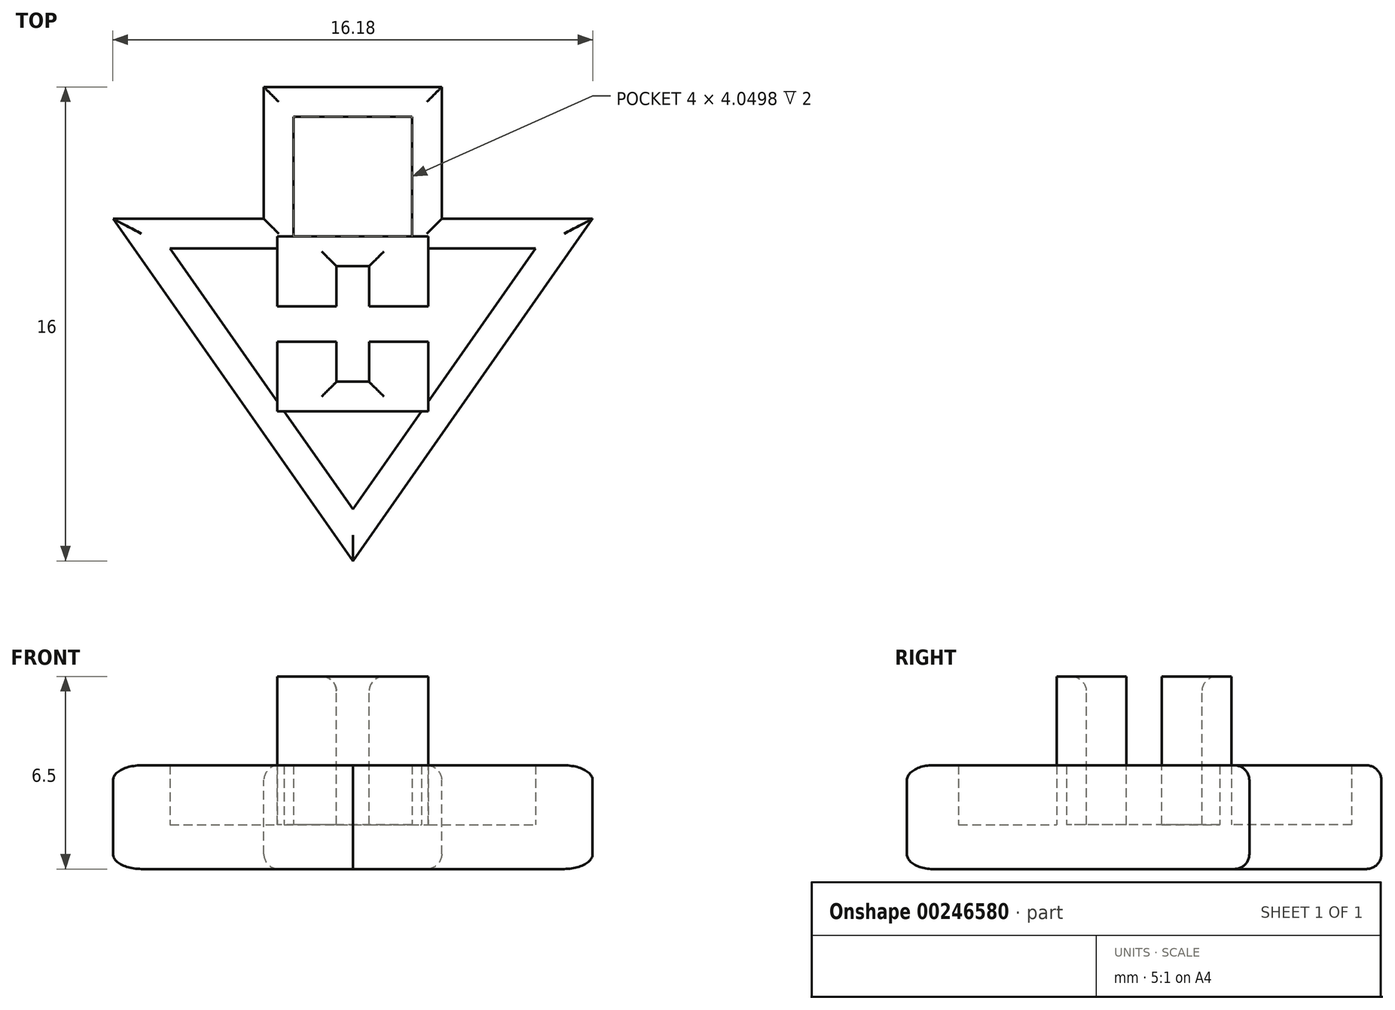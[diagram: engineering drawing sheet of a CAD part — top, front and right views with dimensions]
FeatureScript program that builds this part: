
annotation { "Feature Type Name" : "Feature", "Feature Type Description" : "" }
export const myFeature = defineFeature(function(context is Context, id is Id, definition is map)
    precondition{}
    {
        {
            var Q0;
            Q0=qCreatedBy(makeId("Top.planeOp"),FACE);
            var sketch = newSketch(context, id + "F0", { "sketchPlane" : qUnion([Q0])});
            skLineSegment(sketch, "E0.bottom", {"start": v(-0.55, 1.95) * mm, "end": v(0.55, 1.95) * mm});
            skLineSegment(sketch, "E0.top", {"start": v(-0.55, -1.95) * mm, "end": v(0.55, -1.95) * mm});
            skLineSegment(sketch, "E0.left", {"start": v(-2, 0.6) * mm, "end": v(-2, -0.6) * mm});
            skLineSegment(sketch, "E0.right", {"start": v(2, 0.6) * mm, "end": v(2, -0.6) * mm});
            skPoint(sketch, "E0.middle", {"position": v(0, 0) * mm});
            skLineSegment(sketch, "E1.left", {"start": v(-0.55, 1.95) * mm, "end": v(-0.55, 0.6) * mm});
            skLineSegment(sketch, "E1.right", {"start": v(0.55, 1.95) * mm, "end": v(0.55, 0.6) * mm});
            skLineSegment(sketch, "E2.bottom", {"start": v(-2, 0.6) * mm, "end": v(-0.55, 0.6) * mm});
            skLineSegment(sketch, "E2.top", {"start": v(-2, -0.6) * mm, "end": v(-0.55, -0.6) * mm});
            skLineSegment(sketch, "E3.trimOffspring", {"start": v(-0.55, -0.6) * mm, "end": v(-0.55, -1.95) * mm});
            skLineSegment(sketch, "E4.trimOffspring", {"start": v(0.55, 0.6) * mm, "end": v(2, 0.6) * mm});
            skLineSegment(sketch, "E5.trimOffspring", {"start": v(0.55, -0.6) * mm, "end": v(0.55, -1.95) * mm});
            skLineSegment(sketch, "E6.trimOffspring", {"start": v(0.55, -0.6) * mm, "end": v(2, -0.6) * mm});
            skPoint(sketch, "E7.orphan", {"position": v(-2, 1.95) * mm});
            skPoint(sketch, "E8.orphan", {"position": v(2, 1.95) * mm});
            skPoint(sketch, "E9.orphan", {"position": v(2, -1.95) * mm});
            skPoint(sketch, "E10.orphan", {"position": v(-2, -1.95) * mm});
            skLineSegment(sketch, "E11", {"start": v(-2, 0.6) * mm, "end": v(-2.55, 0.6) * mm});
            skLineSegment(sketch, "E12", {"start": v(-2.55, 0.6) * mm, "end": v(-2.55, 2.95) * mm});
            skLineSegment(sketch, "E13", {"start": v(-2.55, 2.95) * mm, "end": v(0, 2.95) * mm});
            skLineSegment(sketch, "E14.MirrorCS", {"start": v(2.55, 2.95) * mm, "end": v(0, 2.95) * mm});
            skLineSegment(sketch, "E15.MirrorCS", {"start": v(2.55, 0.6) * mm, "end": v(2.55, 2.95) * mm});
            skLineSegment(sketch, "E16.MirrorCS", {"start": v(2, 0.6) * mm, "end": v(2.55, 0.6) * mm});
            skLineSegment(sketch, "E17.MirrorCS", {"start": v(-2, -0.6) * mm, "end": v(-2.55, -0.6) * mm});
            skLineSegment(sketch, "E18.MirrorCS", {"start": v(-2.55, -0.6) * mm, "end": v(-2.55, -2.95) * mm});
            skLineSegment(sketch, "E19.MirrorCS", {"start": v(-2.55, -2.95) * mm, "end": v(0, -2.95) * mm});
            skLineSegment(sketch, "E20.MirrorCS", {"start": v(2.55, -2.95) * mm, "end": v(0, -2.95) * mm});
            skLineSegment(sketch, "E21.MirrorCS", {"start": v(2.55, -0.6) * mm, "end": v(2.55, -2.95) * mm});
            skLineSegment(sketch, "E22.MirrorCS", {"start": v(2, -0.6) * mm, "end": v(2.55, -0.6) * mm});
            skSolve(sketch);
        }
        {
            var Q0;
            Q0=makeQuery(id+"F0.imprint","IMPRINT",FACE,{"disambiguationData":[TD([[makeQuery(id+"F0.imprint","IMPRINT",EDGE,{"derivedFrom":sQuery(id+"F0.wireOp",EDGE,"E0.bottom")}),1.0]])]});
            var Q1;
            Q1=makeQuery(id+"F0.imprint","IMPRINT",FACE,{"disambiguationData":[TD([[makeQuery(id+"F0.imprint","IMPRINT",EDGE,{"derivedFrom":sQuery(id+"F0.wireOp",EDGE,"E0.top")}),-1.0]])]});
            extrude(context, id + "F1", {"entities" : qUnion([Q0, Q1]), "oppositeDirection" : true, "depth" : 5 * mm});
        }
        {
            var Q0;
            Q0=makeQuery(id+"F1.opExtrude","CAP_FACE",FACE,{"disambiguationData":[OSD([sQuery(id+"F0.wireOp",EDGE,"E0.top"),sQuery(id+"F0.wireOp",EDGE,"E2.top"),sQuery(id+"F0.wireOp",EDGE,"E3.trimOffspring"),sQuery(id+"F0.wireOp",EDGE,"E5.trimOffspring"),sQuery(id+"F0.wireOp",EDGE,"E6.trimOffspring"),sQuery(id+"F0.wireOp",EDGE,"E17.MirrorCS"),sQuery(id+"F0.wireOp",EDGE,"E18.MirrorCS"),sQuery(id+"F0.wireOp",EDGE,"E19.MirrorCS"),sQuery(id+"F0.wireOp",EDGE,"E20.MirrorCS"),sQuery(id+"F0.wireOp",EDGE,"E21.MirrorCS"),sQuery(id+"F0.wireOp",EDGE,"E22.MirrorCS")])],"isStart":false});
            var sketch = newSketch(context, id + "F2", { "sketchPlane" : qUnion([Q0])});
            skLineSegment(sketch, "E23", {"start": v(0, 0) * mm, "end": v(0, 8) * mm});
            skLineSegment(sketch, "E24", {"start": v(0, 0) * mm, "end": v(0, -8) * mm});
            skLineSegment(sketch, "E25", {"start": v(0, 8) * mm, "end": v(5.6, 0) * mm});
            skPoint(sketch, "E26.endSnap0", {"position": v(2.95, 0) * mm});
            skLineSegment(sketch, "E27", {"start": v(3, -3.55) * mm, "end": v(3, -8) * mm});
            skLineSegment(sketch, "E28", {"start": v(3, -8) * mm, "end": v(0, -8) * mm});
            skLineSegment(sketch, "E29.MirrorCS", {"start": v(-3, -8) * mm, "end": v(0, -8) * mm});
            skLineSegment(sketch, "E30.MirrorCS", {"start": v(-3, -3.55) * mm, "end": v(-3, -8) * mm});
            skLineSegment(sketch, "E31.MirrorCS", {"start": v(0, 8) * mm, "end": v(-5.6, 0) * mm});
            skLineSegment(sketch, "E32", {"start": v(5.6, 0) * mm, "end": v(8.09, -3.55) * mm});
            skLineSegment(sketch, "E33", {"start": v(8.09, -3.55) * mm, "end": v(3, -3.55) * mm});
            skLineSegment(sketch, "E34.MirrorCS", {"start": v(-8.09, -3.55) * mm, "end": v(-3, -3.55) * mm});
            skLineSegment(sketch, "E35.MirrorCS", {"start": v(-5.6, 0) * mm, "end": v(-8.09, -3.55) * mm});
            skPoint(sketch, "E36.orphan", {"position": v(-2.95, -3.55) * mm});
            skPoint(sketch, "E37.orphan", {"position": v(2.95, -3.55) * mm});
            skPoint(sketch, "E26.end.orphan", {"position": v(3, 0) * mm});
            skPoint(sketch, "E38.orphan", {"position": v(-3, 0) * mm});
            skPoint(sketch, "E39.MirrorCS.start.orphan", {"position": v(-5.6, 0) * mm});
            skPoint(sketch, "E40", {"position": v(0, 0) * mm});
            skSolve(sketch);
        }
        {
            var Q0;
            Q0=makeQuery(id+"F2.imprint","IMPRINT",FACE,{"disambiguationData":[TD([[makeQuery(id+"F2.imprint","IMPRINT",EDGE,{"derivedFrom":sQuery(id+"F2.wireOp",EDGE,"E23")}),-1.0]])]});
            var Q1;
            Q1=makeQuery(id+"F2.imprint","IMPRINT",FACE,{"disambiguationData":[TD([[makeQuery(id+"F2.imprint","IMPRINT",EDGE,{"derivedFrom":sQuery(id+"F2.wireOp",EDGE,"E23")}),1.0]])]});
            var Q2;
            Q2=makeQuery(id+"F2.imprint","IMPRINT",FACE,{"disambiguationData":[TD([[makeQuery(id+"F2.imprint","IMPRINT",EDGE,{"derivedFrom":makeQuery(id+"F1.opExtrude","CAP_EDGE",EDGE,{"disambiguationData":[OSD([sQuery(id+"F0.wireOp",EDGE,"E0.top")])],"isStart":false})}),1.0]])]});
            extrude(context, id + "F3", {"entities" : qUnion([Q0, Q1, Q2]), "operationType" : NewBodyOperationType.ADD, "depth" : 1.5 * mm});
        }
        {
            var Q0;
            Q0=makeQuery(id+"F3.opExtrude","CAP_FACE",FACE,{"disambiguationData":[OSD([sQuery(id+"F2.wireOp",EDGE,"E25"),sQuery(id+"F2.wireOp",EDGE,"E27"),sQuery(id+"F2.wireOp",EDGE,"E28"),sQuery(id+"F2.wireOp",EDGE,"E29.MirrorCS"),sQuery(id+"F2.wireOp",EDGE,"E30.MirrorCS"),sQuery(id+"F2.wireOp",EDGE,"E31.MirrorCS"),sQuery(id+"F2.wireOp",EDGE,"E32"),sQuery(id+"F2.wireOp",EDGE,"E33"),sQuery(id+"F2.wireOp",EDGE,"E34.MirrorCS"),sQuery(id+"F2.wireOp",EDGE,"E35.MirrorCS")])],"isStart":true});
            var sketch = newSketch(context, id + "F4", { "sketchPlane" : qUnion([Q0])});
            skLineSegment(sketch, "E41.0.0", {"start": v(-3, 8) * mm, "end": v(-3, 3.55) * mm});
            skLineSegment(sketch, "E41.0.1", {"start": v(-3, 3.55) * mm, "end": v(-8.09, 3.55) * mm});
            skLineSegment(sketch, "E41.0.2", {"start": v(-8.09, 3.55) * mm, "end": v(0, -8) * mm});
            skLineSegment(sketch, "E41.0.3", {"start": v(0, -8) * mm, "end": v(8.09, 3.55) * mm});
            skLineSegment(sketch, "E41.0.4", {"start": v(8.09, 3.55) * mm, "end": v(3, 3.55) * mm});
            skLineSegment(sketch, "E41.0.5", {"start": v(3, 3.55) * mm, "end": v(3, 8) * mm});
            skLineSegment(sketch, "E41.0.6", {"start": v(3, 8) * mm, "end": v(-3, 8) * mm});
            skLineSegment(sketch, "E42.0", {"start": v(0, -6.26) * mm, "end": v(6.17, 2.55) * mm});
            skLineSegment(sketch, "E43.0", {"start": v(-3, 2.55) * mm, "end": v(-6.17, 2.55) * mm});
            skLineSegment(sketch, "E44.0", {"start": v(2, 3.55) * mm, "end": v(2, 7) * mm});
            skLineSegment(sketch, "E45.0", {"start": v(-2, 7) * mm, "end": v(-2, 3.55) * mm});
            skLineSegment(sketch, "E46.0", {"start": v(2, 7) * mm, "end": v(-2, 7) * mm});
            skLineSegment(sketch, "E47.trimOffspring", {"start": v(6.17, 2.55) * mm, "end": v(3, 2.55) * mm});
            skLineSegment(sketch, "E48.trimOffspring", {"start": v(-6.17, 2.55) * mm, "end": v(0, -6.26) * mm});
            skLineSegment(sketch, "E49", {"start": v(2, 3.55) * mm, "end": v(2, 2.55) * mm});
            skLineSegment(sketch, "E50", {"start": v(2, 2.55) * mm, "end": v(3, 2.55) * mm});
            skLineSegment(sketch, "E51", {"start": v(-2, 3.55) * mm, "end": v(-2, 2.55) * mm});
            skLineSegment(sketch, "E52", {"start": v(-2, 2.55) * mm, "end": v(-3, 2.55) * mm});
            skSolve(sketch);
        }
        {
            var Q0;
            Q0=makeQuery(id+"F4.imprint","IMPRINT",FACE,{"disambiguationData":[TD([[makeQuery(id+"F4.imprint","IMPRINT",EDGE,{"derivedFrom":sQuery(id+"F4.wireOp",EDGE,"E41.0.0")}),-1.0]])]});
            extrude(context, id + "F5", {"entities" : qUnion([Q0]), "operationType" : NewBodyOperationType.ADD, "depth" : 2 * mm});
        }
        {
            var Q0;
            Q0=makeQuery(id+"F3.opExtrude","CAP_EDGE",EDGE,{"disambiguationData":[OSD([sQuery(id+"F2.wireOp",EDGE,"E33")])],"isStart":false});
            var Q1;
            Q1=makeQuery(id+"F3.opExtrude","CAP_EDGE",EDGE,{"disambiguationData":[OSD([sQuery(id+"F2.wireOp",EDGE,"E27")])],"isStart":false});
            var Q2;
            Q2=makeQuery(id+"F3.opExtrude","CAP_EDGE",EDGE,{"disambiguationData":[OSD([sQuery(id+"F2.wireOp",EDGE,"E28"),sQuery(id+"F2.wireOp",EDGE,"E29.MirrorCS")])],"isStart":false});
            var Q3;
            Q3=makeQuery(id+"F3.opExtrude","CAP_EDGE",EDGE,{"disambiguationData":[OSD([sQuery(id+"F2.wireOp",EDGE,"E30.MirrorCS")])],"isStart":false});
            var Q4;
            Q4=makeQuery(id+"F3.opExtrude","CAP_EDGE",EDGE,{"disambiguationData":[OSD([sQuery(id+"F2.wireOp",EDGE,"E34.MirrorCS")])],"isStart":false});
            var Q5;
            Q5=makeQuery(id+"F3.opExtrude","CAP_EDGE",EDGE,{"disambiguationData":[OSD([sQuery(id+"F2.wireOp",EDGE,"E31.MirrorCS"),sQuery(id+"F2.wireOp",EDGE,"E35.MirrorCS")])],"isStart":false});
            var Q6;
            Q6=makeQuery(id+"F3.opExtrude","CAP_EDGE",EDGE,{"disambiguationData":[OSD([sQuery(id+"F2.wireOp",EDGE,"E25"),sQuery(id+"F2.wireOp",EDGE,"E32")])],"isStart":false});
            fillet(context, id + "F6", {"entities" : qUnion([Q0, Q1, Q2, Q3, Q4, Q5, Q6]), "radius" : .5 * mm, "tangentPropagation" : true, "allowEdgeOverflow" : false});
        }
        {
            var Q0;
            Q0=makeQuery(id+"F5.opExtrude","CAP_EDGE",EDGE,{"disambiguationData":[OSD([sQuery(id+"F4.wireOp",EDGE,"E41.0.3")])],"isStart":false});
            var Q1;
            Q1=makeQuery(id+"F5.opExtrude","CAP_EDGE",EDGE,{"disambiguationData":[OSD([sQuery(id+"F4.wireOp",EDGE,"E41.0.2")])],"isStart":false});
            var Q2;
            Q2=makeQuery(id+"F5.opExtrude","CAP_EDGE",EDGE,{"disambiguationData":[OSD([sQuery(id+"F4.wireOp",EDGE,"E41.0.1")])],"isStart":false});
            var Q3;
            Q3=makeQuery(id+"F5.opExtrude","CAP_EDGE",EDGE,{"disambiguationData":[OSD([sQuery(id+"F4.wireOp",EDGE,"E41.0.0")])],"isStart":false});
            var Q4;
            Q4=makeQuery(id+"F5.opExtrude","CAP_EDGE",EDGE,{"disambiguationData":[OSD([sQuery(id+"F4.wireOp",EDGE,"E41.0.6")])],"isStart":false});
            var Q5;
            Q5=makeQuery(id+"F5.opExtrude","CAP_EDGE",EDGE,{"disambiguationData":[OSD([sQuery(id+"F4.wireOp",EDGE,"E41.0.5")])],"isStart":false});
            var Q6;
            Q6=makeQuery(id+"F5.opExtrude","CAP_EDGE",EDGE,{"disambiguationData":[OSD([sQuery(id+"F4.wireOp",EDGE,"E41.0.4")])],"isStart":false});
            fillet(context, id + "F7", {"entities" : qUnion([Q0, Q1, Q2, Q3, Q4, Q5, Q6]), "radius" : .5 * mm, "tangentPropagation" : true, "allowEdgeOverflow" : false});
        }
        {
            var Q0;
            Q0=makeQuery(id+"F1.opExtrude","CAP_EDGE",EDGE,{"disambiguationData":[OSD([sQuery(id+"F0.wireOp",EDGE,"E1.left")])],"isStart":true});
            var Q1;
            Q1=makeQuery(id+"F1.opExtrude","CAP_EDGE",EDGE,{"disambiguationData":[OSD([sQuery(id+"F0.wireOp",EDGE,"E0.bottom")])],"isStart":true});
            var Q2;
            Q2=makeQuery(id+"F1.opExtrude","CAP_EDGE",EDGE,{"disambiguationData":[OSD([sQuery(id+"F0.wireOp",EDGE,"E1.right")])],"isStart":true});
            var Q3;
            Q3=makeQuery(id+"F1.opExtrude","CAP_EDGE",EDGE,{"disambiguationData":[OSD([sQuery(id+"F0.wireOp",EDGE,"E3.trimOffspring")])],"isStart":true});
            var Q4;
            Q4=makeQuery(id+"F1.opExtrude","CAP_EDGE",EDGE,{"disambiguationData":[OSD([sQuery(id+"F0.wireOp",EDGE,"E0.top")])],"isStart":true});
            var Q5;
            Q5=makeQuery(id+"F1.opExtrude","CAP_EDGE",EDGE,{"disambiguationData":[OSD([sQuery(id+"F0.wireOp",EDGE,"E5.trimOffspring")])],"isStart":true});
            fillet(context, id + "F8", {"entities" : qUnion([Q0, Q1, Q2, Q3, Q4, Q5]), "radius" : .5 * mm, "tangentPropagation" : true, "allowEdgeOverflow" : false});
        }
    });
